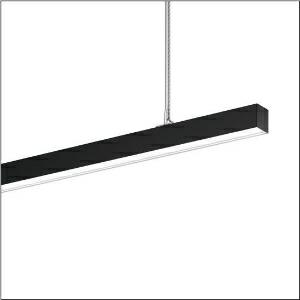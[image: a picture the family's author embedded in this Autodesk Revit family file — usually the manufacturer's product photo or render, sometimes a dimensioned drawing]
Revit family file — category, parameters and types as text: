
# Revit family: silica_r__21_51mx33da37bb_2abf
name_source: partatom
category: Lighting Fixtures
units: mm (PartAtom-declared; Revit-internal decimal feet)

## family parameters
Cut with Voids When Loaded = No
Host = Face
Light Source = No
Part Type = Normal
Room Calculation Point = No
Round Connector Dimension = Use Diameter
Shared = No

## types (1)
- --- (1 x LED, 5910 lm, 41.3 W, 3000K)
    Apparent Load = 41 VA
    CIE Flux Codes = 78 96 99 55 100
    Color Rendering = 80
    Color Temperature = 3000K
    Default Elevation = 1800 mm
    Description = Silica® 21, office luminaire, primary optical cover: prismatic diffuser, of PMMA, CAT 2 (L<= 3000cd/m²), light emission: direct/indirect distribution, primary light characteristic: symmetric, installation type: suspended mounting, LED, rated luminous flux: 5.910lm, luminous efficacy: 143lm/W, light colour: 830, colour temperature: 3000K, control gear: DALI 2, with terminal, 3+2-pole, max. 2.5mm², mains connection: 220..240V, AC, 50/60Hz, rated input power: 41.3W, luminaire housing, of aluminium, matt jet black (RAL 9005), length: 1.204mm, width: 53mm, height: 53mm, protection rating (complete): IP20, insulation class (complete): insulation class I (protective earthing), certification: CE, permissible operating ambient temperature: 0..+35°C, standard: EN 50419, packaging unit: 1 piece
    Height = 53 mm
    Lamp = 1 x LED
    Lamp Light Flux = 5910 lm
    Lamp Power = 41.3 W
    Lamp count = 1
    Length = 1204 mm
    Luminous efficacy = 143 lm/W
    Manufacturer = Siteco
    ModVariant = No
    Model = 51MX33DA37BB
    Mounting Place = Ceiling
    Mounting Type = Pendant
    Number of Poles = 1
    OnlyDefault = Yes
    Power Factor = 1
    Product Name = Silica® 21
    Product group = office luminaire | ceiling pendant
    ProductGroupID = 904
    Protection Class = Protection class I
    Protection Degree = IP 20
    RLX_Detail_Level = 1
    RLX_Emergency_Light_Flux = 0 lm
    RLX_Emergency_Type = 0
    RLX_Emergency_Type_DB = No
    RlxData = <blob elided: 26213 chars, md5=82f31554>
    Socket = socket
    Standby Power = 0 W
    System Light Flux = 5910 lm
    System Power = 41 W
    Type Comments = factory setting: luminous flux: 100 % | dim-lin: 254 | 345 mA
    Type Image = l_1335856.jpg
    URL = http://relux.com
    VarID = @adj_118712
    Voltage = 0 V
    Weight = 0.00 kg
    Width = 53 mm

## geometry (parser evidence)
native form markers: Blend x4, Sweep x15
no freeform markers — native parametric forms only
